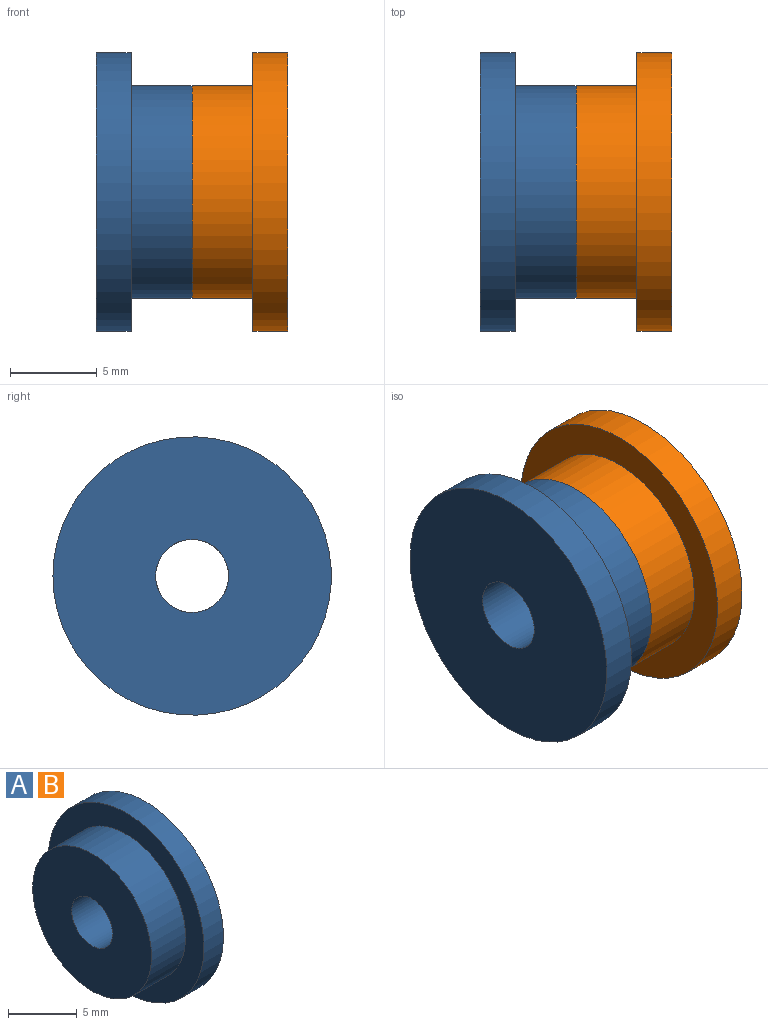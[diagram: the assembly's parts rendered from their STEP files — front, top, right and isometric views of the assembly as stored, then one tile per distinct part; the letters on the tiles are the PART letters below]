
ASSEMBLY  parts=2 mates=1
PART A: 6 faces, bbox 5.5x16x16 mm
  f0: plane 16x16mm, normal (1,0,0), area 187.2mm2, adj f1,f4
  f1: cylinder r=2.1mm len=5.5mm, axis (-1,0,0), area 72.6mm2, adj f0,f3
  f2: plane 16x16mm, normal (-1,0,0), area 83.8mm2, adj f4,f5
  f3: plane 12.22x12.22mm, normal (-1,0,0), area 103.4mm2, adj f1,f5
  f4: cylinder r=8mm len=16mm, axis (-1,0,0), area 100.5mm2, adj f0,f2
  f5: cylinder r=6.11mm len=12.22mm, axis (1,0,0), area 134.4mm2, adj f2,f3
PART B: same geometry as A
PLACE A rot(axis=(0,1,0),180deg) t=(-6.35,-0.85,-1.18)mm
PLACE B t=(0.65,-0.85,-1.18)mm
MATE fastened A.f1 <-> B.f1  axis (1,0,0) through (-2.85,-0.85,-1.18)mm
